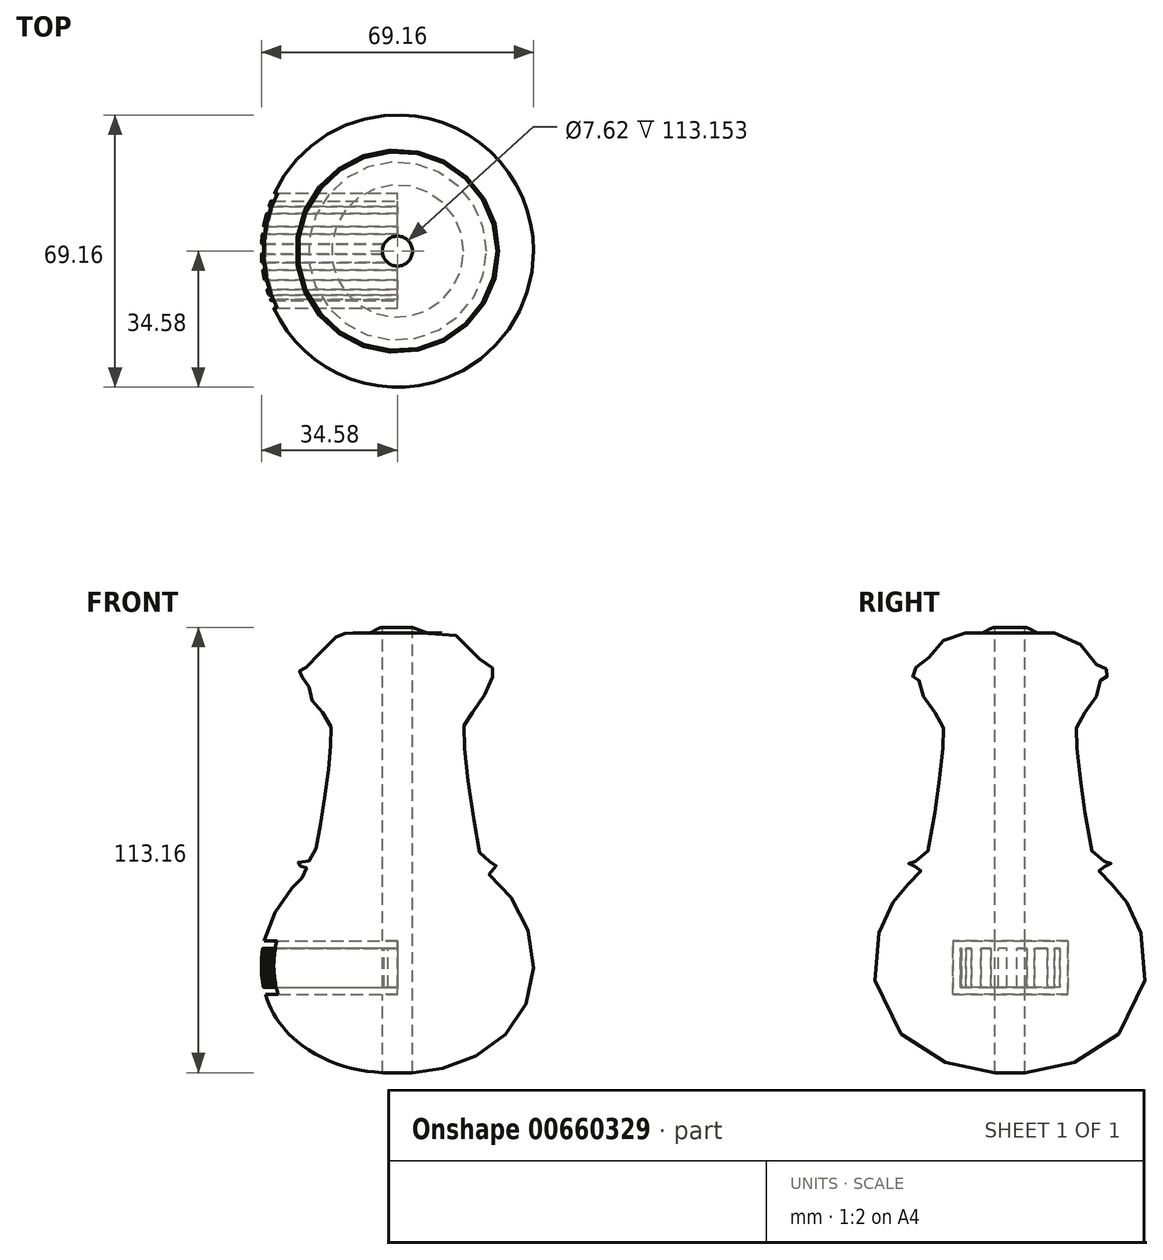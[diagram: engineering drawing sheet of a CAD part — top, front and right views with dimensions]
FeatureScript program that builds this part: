
annotation { "Feature Type Name" : "Feature", "Feature Type Description" : "" }
export const myFeature = defineFeature(function(context is Context, id is Id, definition is map)
    precondition{}
    {
        {
            var Q0;
            Q0=qCreatedBy(makeId("Front.planeOp"),FACE);
            var sketch = newSketch(context, id + "F0", { "sketchPlane" : qUnion([Q0])});
            skLineSegment(sketch, "E0", {"start": v(0, 30.64) * mm, "end": v(0, -86) * mm});
            skFitSpline(sketch, "E1", {"points": [v(0, 30.64) * mm, v(1.97, 30.64) * mm, v(0.8, 27.94) * mm, v(4.21, 27.2) * mm, v(7.2, 25.8) * mm, v(15.41, 24.95) * mm, v(22.56, 17.28) * mm, v(24.05, 16.96) * mm, v(25.22, 15.04) * mm, v(23.52, 14.4) * mm, v(21.6, 8.53) * mm, v(18.61, 5.23) * mm, v(17.12, 3) * mm, v(16.9, -2.23) * mm, v(18.4, -15.26) * mm, v(20.9, -29.88) * mm, v(22.1, -31.94) * mm, v(25.02, -32.37) * mm, v(25.67, -33.02) * mm, v(22.74, -34.1) * mm, v(26.2, -38.33) * mm, v(33.66, -51.6) * mm, v(33.04, -67.55) * mm, v(23.4, -79.56) * mm, v(9.87, -85.17) * mm, v(0, -86) * mm], "startDerivative": vector(124.74, 27.96) * mm, "endDerivative": vector(-180.34, -3.36) * mm});
            skSolve(sketch);
        }
        {
            var Q0;
            Q0 = qSketchRegion(id + "F0", true);
            var Q1;
            Q1=sQuery(id+"F0.wireOp",EDGE,"E0");
            revolve(context, id + "F1", {"entities" : qUnion([Q0]), "axis" : qUnion([Q1]), "revolveType" : RevolveType.FULL});
        }
        {
            var Q0;
            Q0=qCreatedBy(makeId("Top.planeOp"),FACE);
            var sketch = newSketch(context, id + "F2", { "sketchPlane" : qUnion([Q0])});
            skCircle(sketch, "E2", {"center": v(0, 0) * mm, "radius": 3.81 * mm});
            skSolve(sketch);
        }
        {
            var Q0;
            Q0 = qSketchRegion(id + "F2", true);
            extrude(context, id + "F3", {"entities" : qUnion([Q0]), "operationType" : NewBodyOperationType.REMOVE, "endBound" : BoundingType.SYMMETRIC, "oppositeDirection" : true, "depth" : 254 * mm, "offsetDistance" : 25.4 * mm});
        }
        {
            var Q0;
            Q0=qCreatedBy(makeId("Right.planeOp"),FACE);
            var sketch = newSketch(context, id + "F4", { "sketchPlane" : qUnion([Q0])});
            skLineSegment(sketch, "E3.bottom", {"start": v(-14.45, -52.47) * mm, "end": v(14.76, -52.47) * mm});
            skLineSegment(sketch, "E3.top", {"start": v(-14.45, -66.06) * mm, "end": v(14.76, -66.06) * mm});
            skLineSegment(sketch, "E3.left", {"start": v(-14.45, -52.47) * mm, "end": v(-14.45, -66.06) * mm});
            skLineSegment(sketch, "E3.right", {"start": v(14.76, -52.47) * mm, "end": v(14.76, -66.06) * mm});
            skLineSegment(sketch, "E4.bottom", {"start": v(-12.6, -54.31) * mm, "end": v(12.74, -54.31) * mm});
            skLineSegment(sketch, "E4.top", {"start": v(-12.6, -64.22) * mm, "end": v(12.74, -64.22) * mm});
            skLineSegment(sketch, "E4.left", {"start": v(-12.6, -54.31) * mm, "end": v(-12.6, -64.22) * mm});
            skLineSegment(sketch, "E4.right", {"start": v(12.74, -54.31) * mm, "end": v(12.74, -64.22) * mm});
            skSolve(sketch);
        }
        {
            var Q0;
            Q0 = qSketchRegion(id + "F4", true);
            extrude(context, id + "F5", {"entities" : qUnion([Q0]), "operationType" : NewBodyOperationType.REMOVE, "oppositeDirection" : true, "depth" : 38.1 * mm, "offsetDistance" : 25.4 * mm});
        }
        {
            var Q0;
            Q0=qCreatedBy(makeId("Right.planeOp"),FACE);
            var sketch = newSketch(context, id + "F6", { "sketchPlane" : qUnion([Q0])});
            skLineSegment(sketch, "E5.bottom", {"start": v(11.32, -54.25) * mm, "end": v(9.49, -54.25) * mm});
            skLineSegment(sketch, "E5.top", {"start": v(11.32, -64.18) * mm, "end": v(9.49, -64.18) * mm});
            skLineSegment(sketch, "E5.left", {"start": v(11.32, -54.25) * mm, "end": v(11.32, -64.18) * mm});
            skLineSegment(sketch, "E5.right", {"start": v(9.49, -54.25) * mm, "end": v(9.49, -64.18) * mm});
            skLineSegment(sketch, "E6.bottom", {"start": v(6.2, -54.25) * mm, "end": v(4.38, -54.25) * mm});
            skLineSegment(sketch, "E6.top", {"start": v(6.2, -64.18) * mm, "end": v(4.38, -64.18) * mm});
            skLineSegment(sketch, "E6.left", {"start": v(6.2, -54.25) * mm, "end": v(6.2, -64.18) * mm});
            skLineSegment(sketch, "E6.right", {"start": v(4.38, -54.25) * mm, "end": v(4.38, -64.18) * mm});
            skLineSegment(sketch, "E7.bottom", {"start": v(1.77, -54.25) * mm, "end": v(-0.73, -54.25) * mm});
            skLineSegment(sketch, "E7.top", {"start": v(1.77, -64.18) * mm, "end": v(-0.73, -64.18) * mm});
            skLineSegment(sketch, "E7.left", {"start": v(1.77, -54.25) * mm, "end": v(1.77, -64.18) * mm});
            skLineSegment(sketch, "E7.right", {"start": v(-0.73, -54.25) * mm, "end": v(-0.73, -64.18) * mm});
            skLineSegment(sketch, "E8.bottom", {"start": v(-4.88, -54.25) * mm, "end": v(-2.95, -54.25) * mm});
            skLineSegment(sketch, "E8.top", {"start": v(-4.88, -64.18) * mm, "end": v(-2.95, -64.18) * mm});
            skLineSegment(sketch, "E8.left", {"start": v(-4.88, -54.25) * mm, "end": v(-4.88, -64.18) * mm});
            skLineSegment(sketch, "E8.right", {"start": v(-2.95, -54.25) * mm, "end": v(-2.95, -64.18) * mm});
            skLineSegment(sketch, "E9.bottom", {"start": v(-7.38, -54.25) * mm, "end": v(-9.8, -54.25) * mm});
            skLineSegment(sketch, "E9.top", {"start": v(-7.38, -64.18) * mm, "end": v(-9.8, -64.18) * mm});
            skLineSegment(sketch, "E9.left", {"start": v(-7.38, -54.25) * mm, "end": v(-7.38, -64.18) * mm});
            skLineSegment(sketch, "E9.right", {"start": v(-9.8, -54.25) * mm, "end": v(-9.8, -64.18) * mm});
            skLineSegment(sketch, "E10.bottom", {"start": v(-11.14, -54.25) * mm, "end": v(-12.3, -54.25) * mm});
            skLineSegment(sketch, "E10.top", {"start": v(-11.14, -64.18) * mm, "end": v(-12.3, -64.18) * mm});
            skLineSegment(sketch, "E10.left", {"start": v(-11.14, -54.25) * mm, "end": v(-11.14, -64.18) * mm});
            skLineSegment(sketch, "E10.right", {"start": v(-12.3, -54.25) * mm, "end": v(-12.3, -64.18) * mm});
            skSolve(sketch);
        }
        {
            var Q0;
            Q0 = qSketchRegion(id + "F6", true);
            extrude(context, id + "F7", {"entities" : qUnion([Q0]), "operationType" : NewBodyOperationType.REMOVE, "oppositeDirection" : true, "depth" : 38.1 * mm, "offsetDistance" : 25.4 * mm});
        }
    });
